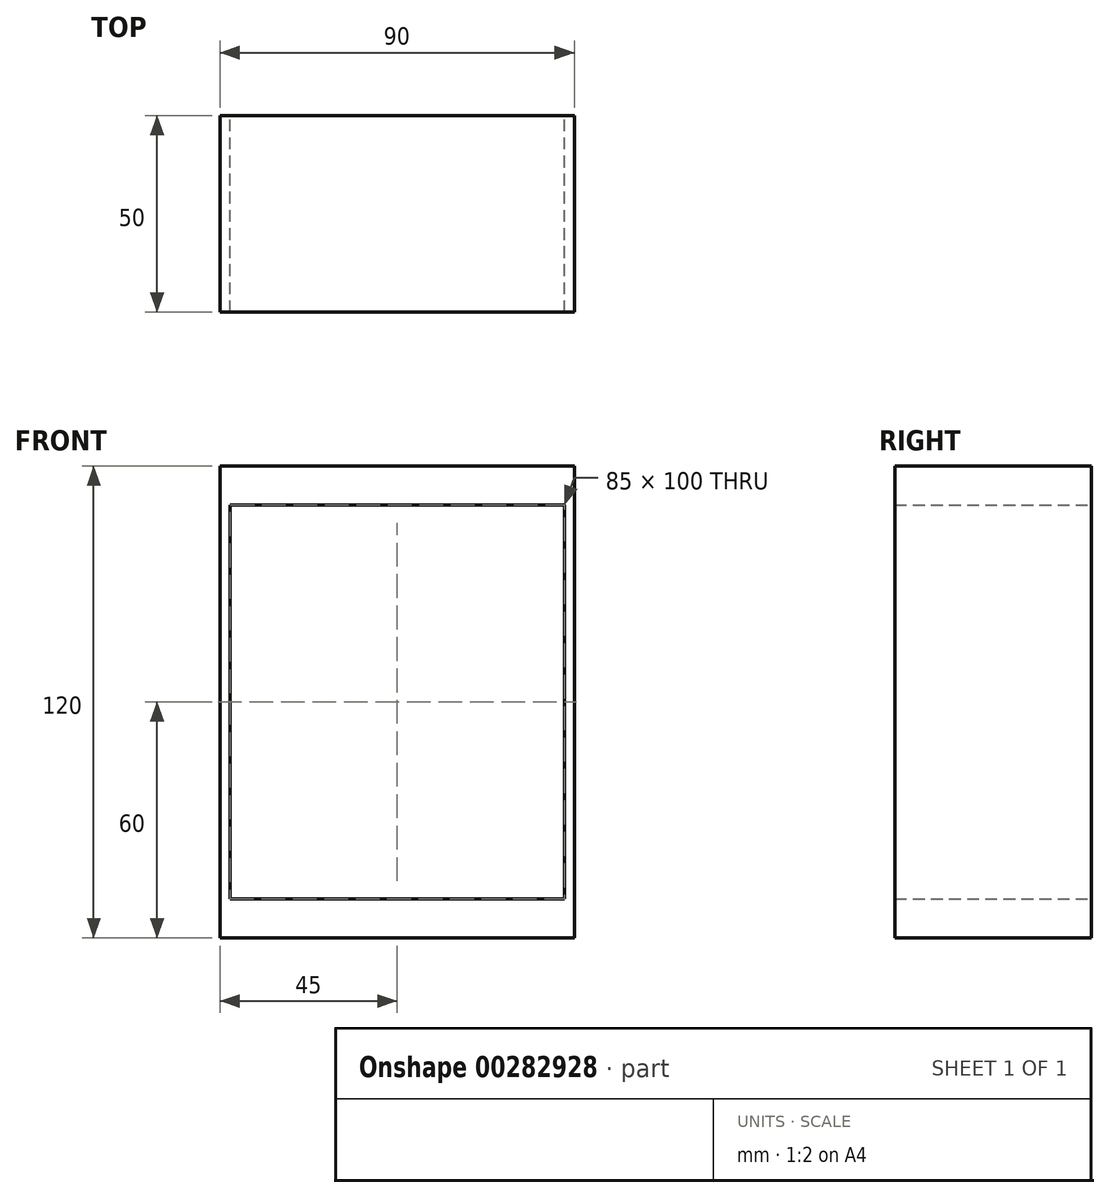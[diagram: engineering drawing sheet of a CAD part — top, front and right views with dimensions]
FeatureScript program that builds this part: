
annotation { "Feature Type Name" : "Feature", "Feature Type Description" : "" }
export const myFeature = defineFeature(function(context is Context, id is Id, definition is map)
    precondition{}
    {
        {
            var Q0;
            Q0=qCreatedBy(makeId("Front.planeOp"),FACE);
            var sketch = newSketch(context, id + "F0", { "sketchPlane" : qUnion([Q0])});
            skLineSegment(sketch, "E0.bottom", {"start": v(-45, 60) * mm, "end": v(45, 60) * mm});
            skLineSegment(sketch, "E0.top", {"start": v(-45, -60) * mm, "end": v(45, -60) * mm});
            skLineSegment(sketch, "E0.left", {"start": v(-45, 60) * mm, "end": v(-45, -60) * mm});
            skLineSegment(sketch, "E0.right", {"start": v(45, 60) * mm, "end": v(45, -60) * mm});
            skPoint(sketch, "E0.middle", {"position": v(0, 0) * mm});
            skLineSegment(sketch, "E1.bottom", {"start": v(-42.5, 50) * mm, "end": v(42.5, 50) * mm});
            skLineSegment(sketch, "E1.top", {"start": v(-42.5, -50) * mm, "end": v(42.5, -50) * mm});
            skLineSegment(sketch, "E1.left", {"start": v(-42.5, 50) * mm, "end": v(-42.5, -50) * mm});
            skLineSegment(sketch, "E1.right", {"start": v(42.5, 50) * mm, "end": v(42.5, -50) * mm});
            skSolve(sketch);
        }
        {
            var Q0;
            Q0=makeQuery(id+"F0.imprint","IMPRINT",FACE,{"disambiguationData":[TD([[makeQuery(id+"F0.imprint","IMPRINT",EDGE,{"derivedFrom":sQuery(id+"F0.wireOp",EDGE,"E0.bottom")}),-1.0]])]});
            extrude(context, id + "F1", {"entities" : qUnion([Q0]), "depth" : 50 * mm});
        }
    });
